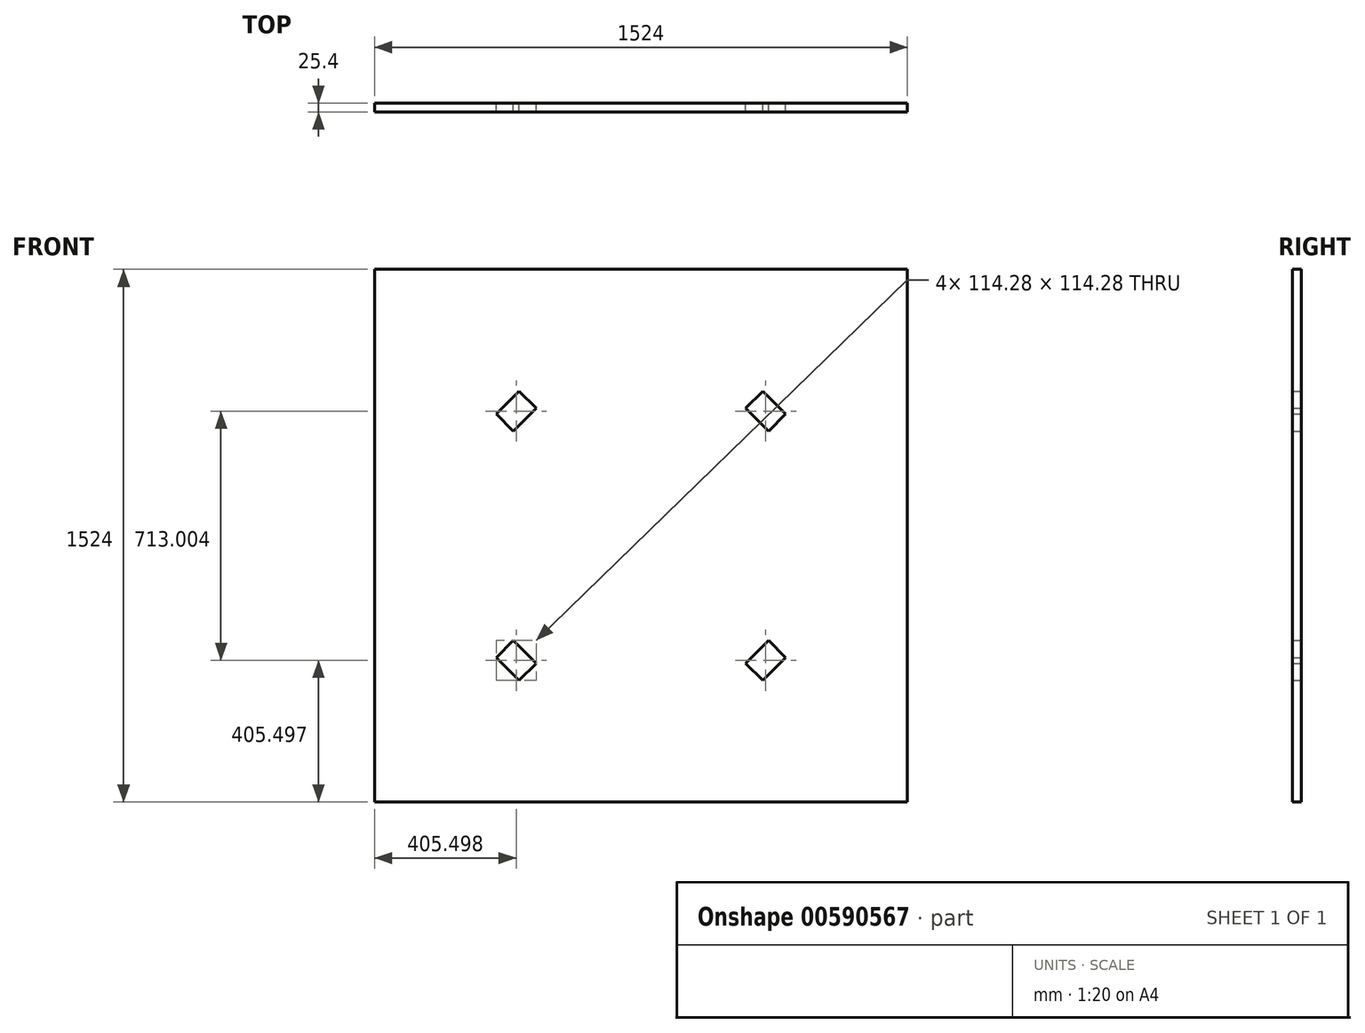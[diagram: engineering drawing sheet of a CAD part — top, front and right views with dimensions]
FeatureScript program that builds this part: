
annotation { "Feature Type Name" : "Feature", "Feature Type Description" : "" }
export const myFeature = defineFeature(function(context is Context, id is Id, definition is map)
    precondition{}
    {
        {
            var Q0;
            Q0=qCreatedBy(makeId("Front.planeOp"),FACE);
            var sketch = newSketch(context, id + "F0", { "sketchPlane" : qUnion([Q0])});
            skLineSegment(sketch, "E0.bottom", {"start": v(-611.02, 817.16) * mm, "end": v(912.98, 817.16) * mm});
            skLineSegment(sketch, "E0.top", {"start": v(-611.02, -706.84) * mm, "end": v(912.98, -706.84) * mm});
            skLineSegment(sketch, "E0.left", {"start": v(-611.02, 817.16) * mm, "end": v(-611.02, -706.84) * mm});
            skLineSegment(sketch, "E0.right", {"start": v(912.98, 817.16) * mm, "end": v(912.98, -706.84) * mm});
            skLineSegment(sketch, "E1.bottom", {"start": v(608.18, -402.04) * mm, "end": v(-306.22, -402.04) * mm});
            skLineSegment(sketch, "E1.top", {"start": v(608.18, 512.36) * mm, "end": v(-306.22, 512.36) * mm});
            skLineSegment(sketch, "E1.left", {"start": v(608.18, -402.04) * mm, "end": v(608.18, 512.36) * mm});
            skLineSegment(sketch, "E1.right", {"start": v(-306.22, -402.04) * mm, "end": v(-306.22, 512.36) * mm});
            skPoint(sketch, "E1.middle", {"position": v(150.98, 55.16) * mm});
            skPoint(sketch, "E1.middle.positionSnap0", {"position": v(-611.02, 55.16) * mm});
            skPoint(sketch, "E1.middle.positionSnap1", {"position": v(150.98, 817.16) * mm});
            skPoint(sketch, "E1.centerSnap0", {"position": v(-611.02, 55.16) * mm});
            skPoint(sketch, "E1.centerSnap1", {"position": v(150.98, 817.16) * mm});
            skLineSegment(sketch, "E2.bottom", {"start": v(-306.22, 512.36) * mm, "end": v(-1.42, 512.36) * mm});
            skLineSegment(sketch, "E2.top", {"start": v(-306.22, 817.16) * mm, "end": v(-1.42, 817.16) * mm});
            skLineSegment(sketch, "E3.bottom", {"start": v(-26.82, 537.76) * mm, "end": v(-280.82, 537.76) * mm});
            skLineSegment(sketch, "E3.top", {"start": v(-26.82, 791.76) * mm, "end": v(-280.82, 791.76) * mm});
            skLineSegment(sketch, "E3.left", {"start": v(-26.82, 537.76) * mm, "end": v(-26.82, 791.76) * mm});
            skLineSegment(sketch, "E3.right", {"start": v(-280.82, 537.76) * mm, "end": v(-280.82, 791.76) * mm});
            skPoint(sketch, "E3.middle", {"position": v(-153.82, 664.76) * mm});
            skPoint(sketch, "E3.middle.positionSnap0", {"position": v(-153.82, 817.16) * mm});
            skPoint(sketch, "E3.middle.positionSnap1", {"position": v(-1.42, 664.76) * mm});
            skPoint(sketch, "E3.centerSnap0", {"position": v(-153.82, 817.16) * mm});
            skPoint(sketch, "E3.centerSnap1", {"position": v(-1.42, 664.76) * mm});
            skLineSegment(sketch, "E4.left", {"start": v(-306.22, 512.36) * mm, "end": v(-306.22, 207.56) * mm});
            skLineSegment(sketch, "E4.right", {"start": v(-611.02, 512.36) * mm, "end": v(-611.02, 207.56) * mm});
            skLineSegment(sketch, "E5.bottom", {"start": v(-331.62, 486.96) * mm, "end": v(-585.62, 486.96) * mm});
            skLineSegment(sketch, "E5.top", {"start": v(-331.62, 232.96) * mm, "end": v(-585.62, 232.96) * mm});
            skLineSegment(sketch, "E5.left", {"start": v(-331.62, 486.96) * mm, "end": v(-331.62, 232.96) * mm});
            skLineSegment(sketch, "E5.right", {"start": v(-585.62, 486.96) * mm, "end": v(-585.62, 232.96) * mm});
            skPoint(sketch, "E5.middle", {"position": v(-458.62, 359.96) * mm});
            skPoint(sketch, "E5.middle.positionSnap0", {"position": v(-458.62, 512.36) * mm});
            skPoint(sketch, "E5.middle.positionSnap1", {"position": v(-306.22, 359.96) * mm});
            skPoint(sketch, "E5.centerSnap0", {"position": v(-458.62, 512.36) * mm});
            skPoint(sketch, "E5.centerSnap1", {"position": v(-306.22, 359.96) * mm});
            skLineSegment(sketch, "E6.MirrorCS", {"start": v(-331.62, -122.64) * mm, "end": v(-585.62, -122.64) * mm});
            skLineSegment(sketch, "E7.MirrorCS", {"start": v(-331.62, -376.64) * mm, "end": v(-331.62, -122.64) * mm});
            skLineSegment(sketch, "E8.MirrorCS", {"start": v(-331.62, -376.64) * mm, "end": v(-585.62, -376.64) * mm});
            skLineSegment(sketch, "E9.MirrorCS", {"start": v(-585.62, -376.64) * mm, "end": v(-585.62, -122.64) * mm});
            skLineSegment(sketch, "E10.MirrorCS", {"start": v(-26.82, -427.44) * mm, "end": v(-280.82, -427.44) * mm});
            skLineSegment(sketch, "E11.MirrorCS", {"start": v(-26.82, -427.44) * mm, "end": v(-26.82, -681.44) * mm});
            skLineSegment(sketch, "E12.MirrorCS", {"start": v(-26.82, -681.44) * mm, "end": v(-280.82, -681.44) * mm});
            skLineSegment(sketch, "E13.MirrorCS", {"start": v(-280.82, -427.44) * mm, "end": v(-280.82, -681.44) * mm});
            skLineSegment(sketch, "E14.MirrorCS", {"start": v(328.78, 537.76) * mm, "end": v(328.78, 791.76) * mm});
            skLineSegment(sketch, "E15.MirrorCS", {"start": v(328.78, 791.76) * mm, "end": v(582.78, 791.76) * mm});
            skLineSegment(sketch, "E16.MirrorCS", {"start": v(582.78, 537.76) * mm, "end": v(582.78, 791.76) * mm});
            skLineSegment(sketch, "E17.MirrorCS", {"start": v(633.58, 486.96) * mm, "end": v(633.58, 232.96) * mm});
            skLineSegment(sketch, "E18.MirrorCS", {"start": v(633.58, 486.96) * mm, "end": v(887.58, 486.96) * mm});
            skLineSegment(sketch, "E19.MirrorCS", {"start": v(887.58, 486.96) * mm, "end": v(887.58, 232.96) * mm});
            skLineSegment(sketch, "E20.MirrorCS", {"start": v(633.58, 232.96) * mm, "end": v(887.58, 232.96) * mm});
            skLineSegment(sketch, "E21.MirrorCS", {"start": v(328.78, 537.76) * mm, "end": v(582.78, 537.76) * mm});
            skLineSegment(sketch, "E22.MirrorCS", {"start": v(328.78, -427.44) * mm, "end": v(582.78, -427.44) * mm});
            skLineSegment(sketch, "E23.MirrorCS", {"start": v(582.78, -427.44) * mm, "end": v(582.78, -681.44) * mm});
            skLineSegment(sketch, "E24.MirrorCS", {"start": v(328.78, -681.44) * mm, "end": v(582.78, -681.44) * mm});
            skLineSegment(sketch, "E25.MirrorCS", {"start": v(328.78, -427.44) * mm, "end": v(328.78, -681.44) * mm});
            skLineSegment(sketch, "E26.MirrorCS", {"start": v(633.58, -376.64) * mm, "end": v(887.58, -376.64) * mm});
            skLineSegment(sketch, "E27.MirrorCS", {"start": v(633.58, -376.64) * mm, "end": v(633.58, -122.64) * mm});
            skLineSegment(sketch, "E28.MirrorCS", {"start": v(887.58, -376.64) * mm, "end": v(887.58, -122.64) * mm});
            skLineSegment(sketch, "E29.MirrorCS", {"start": v(633.58, -122.64) * mm, "end": v(887.58, -122.64) * mm});
            skLineSegment(sketch, "E30.bottom", {"start": v(582.78, 486.96) * mm, "end": v(-280.82, 486.96) * mm});
            skLineSegment(sketch, "E30.top", {"start": v(582.78, -376.64) * mm, "end": v(-280.82, -376.64) * mm});
            skLineSegment(sketch, "E30.left", {"start": v(582.78, 486.96) * mm, "end": v(582.78, -376.64) * mm});
            skLineSegment(sketch, "E30.right", {"start": v(-280.82, 486.96) * mm, "end": v(-280.82, -376.64) * mm});
            skLineSegment(sketch, "E31", {"start": v(-280.82, 486.96) * mm, "end": v(-179.22, 486.96) * mm});
            skLineSegment(sketch, "E32", {"start": v(-280.82, 486.96) * mm, "end": v(-280.82, 385.36) * mm});
            skLineSegment(sketch, "E33", {"start": v(-197.38, 468.8) * mm, "end": v(-230.02, 436.16) * mm});
            skLineSegment(sketch, "E34", {"start": v(-230.02, 436.16) * mm, "end": v(-197.38, 468.8) * mm});
            skLineSegment(sketch, "E35", {"start": v(-230.02, 436.16) * mm, "end": v(-262.66, 403.52) * mm});
            skLineSegment(sketch, "E36", {"start": v(-262.66, 403.52) * mm, "end": v(-213.67, 354.52) * mm});
            skLineSegment(sketch, "E37", {"start": v(-213.67, 354.52) * mm, "end": v(-148.38, 419.8) * mm});
            skLineSegment(sketch, "E38", {"start": v(-197.38, 468.8) * mm, "end": v(-148.38, 419.8) * mm});
            skLineSegment(sketch, "E39.MirrorCS", {"start": v(515.63, 354.52) * mm, "end": v(450.34, 419.8) * mm});
            skLineSegment(sketch, "E40.MirrorCS", {"start": v(564.62, 403.52) * mm, "end": v(515.63, 354.52) * mm});
            skLineSegment(sketch, "E41.MirrorCS", {"start": v(531.98, 436.16) * mm, "end": v(564.62, 403.52) * mm});
            skLineSegment(sketch, "E42.MirrorCS", {"start": v(499.34, 468.8) * mm, "end": v(531.98, 436.16) * mm});
            skLineSegment(sketch, "E43.MirrorCS", {"start": v(499.34, 468.8) * mm, "end": v(450.34, 419.8) * mm});
            skLineSegment(sketch, "E44.MirrorCS", {"start": v(-213.67, -244.2) * mm, "end": v(-148.38, -309.49) * mm});
            skLineSegment(sketch, "E45.MirrorCS", {"start": v(-262.66, -293.2) * mm, "end": v(-213.67, -244.2) * mm});
            skLineSegment(sketch, "E46.MirrorCS", {"start": v(-197.38, -358.48) * mm, "end": v(-148.38, -309.49) * mm});
            skLineSegment(sketch, "E47.MirrorCS", {"start": v(-197.38, -358.48) * mm, "end": v(-230.02, -325.84) * mm});
            skLineSegment(sketch, "E48.MirrorCS", {"start": v(-230.02, -325.84) * mm, "end": v(-262.66, -293.2) * mm});
            skLineSegment(sketch, "E49.MirrorCS", {"start": v(515.63, -244.2) * mm, "end": v(450.34, -309.49) * mm});
            skLineSegment(sketch, "E50.MirrorCS", {"start": v(499.34, -358.48) * mm, "end": v(450.34, -309.49) * mm});
            skLineSegment(sketch, "E51.MirrorCS", {"start": v(499.34, -358.48) * mm, "end": v(531.98, -325.84) * mm});
            skLineSegment(sketch, "E52.MirrorCS", {"start": v(564.62, -293.2) * mm, "end": v(515.63, -244.2) * mm});
            skLineSegment(sketch, "E53.MirrorCS", {"start": v(531.98, -325.84) * mm, "end": v(564.62, -293.2) * mm});
            skSolve(sketch);
        }
        {
            var Q0;
            Q0 = qSketchRegion(id + "F0", true);
            var Q1;
            Q1=makeQuery(id+"F0.imprint","IMPRINT",FACE,{"disambiguationData":[TD([[makeQuery(id+"F0.imprint","IMPRINT",EDGE,{"derivedFrom":sQuery(id+"F0.wireOp",EDGE,"E5.bottom")}),1.0]])]});
            var Q2;
            Q2=makeQuery(id+"F0.imprint","IMPRINT",FACE,{"disambiguationData":[TD([[makeQuery(id+"F0.imprint","IMPRINT",EDGE,{"derivedFrom":sQuery(id+"F0.wireOp",EDGE,"E3.bottom")}),-1.0]])]});
            var Q3;
            Q3=makeQuery(id+"F0.imprint","IMPRINT",FACE,{"disambiguationData":[TD([[makeQuery(id+"F0.imprint","IMPRINT",EDGE,{"derivedFrom":sQuery(id+"F0.wireOp",EDGE,"E14.MirrorCS")}),-1.0]])]});
            var Q4;
            Q4=makeQuery(id+"F0.imprint","IMPRINT",FACE,{"disambiguationData":[TD([[makeQuery(id+"F0.imprint","IMPRINT",EDGE,{"derivedFrom":sQuery(id+"F0.wireOp",EDGE,"E30.bottom")}),1.0]])]});
            var Q5;
            Q5=makeQuery(id+"F0.imprint","IMPRINT",FACE,{"disambiguationData":[TD([[makeQuery(id+"F0.imprint","IMPRINT",EDGE,{"derivedFrom":sQuery(id+"F0.wireOp",EDGE,"E17.MirrorCS")}),1.0]])]});
            var Q6;
            Q6=makeQuery(id+"F0.imprint","IMPRINT",FACE,{"disambiguationData":[TD([[makeQuery(id+"F0.imprint","IMPRINT",EDGE,{"derivedFrom":sQuery(id+"F0.wireOp",EDGE,"E26.MirrorCS")}),1.0]])]});
            var Q7;
            Q7=makeQuery(id+"F0.imprint","IMPRINT",FACE,{"disambiguationData":[TD([[makeQuery(id+"F0.imprint","IMPRINT",EDGE,{"derivedFrom":sQuery(id+"F0.wireOp",EDGE,"E1.bottom")}),-1.0]])]});
            var Q8;
            Q8=makeQuery(id+"F0.imprint","IMPRINT",FACE,{"disambiguationData":[TD([[makeQuery(id+"F0.imprint","IMPRINT",EDGE,{"derivedFrom":sQuery(id+"F0.wireOp",EDGE,"E22.MirrorCS")}),-1.0]])]});
            var Q9;
            Q9=makeQuery(id+"F0.imprint","IMPRINT",FACE,{"disambiguationData":[TD([[makeQuery(id+"F0.imprint","IMPRINT",EDGE,{"derivedFrom":sQuery(id+"F0.wireOp",EDGE,"E10.MirrorCS")}),1.0]])]});
            var Q10;
            Q10=makeQuery(id+"F0.imprint","IMPRINT",FACE,{"disambiguationData":[TD([[makeQuery(id+"F0.imprint","IMPRINT",EDGE,{"derivedFrom":sQuery(id+"F0.wireOp",EDGE,"E6.MirrorCS")}),1.0]])]});
            extrude(context, id + "F1", {"entities" : qUnion([Q0, Q1, Q2, Q3, Q4, Q5, Q6, Q7, Q8, Q9, Q10]), "depth" : 25.4 * mm, "offsetDistance" : 25.4 * mm});
        }
    });
